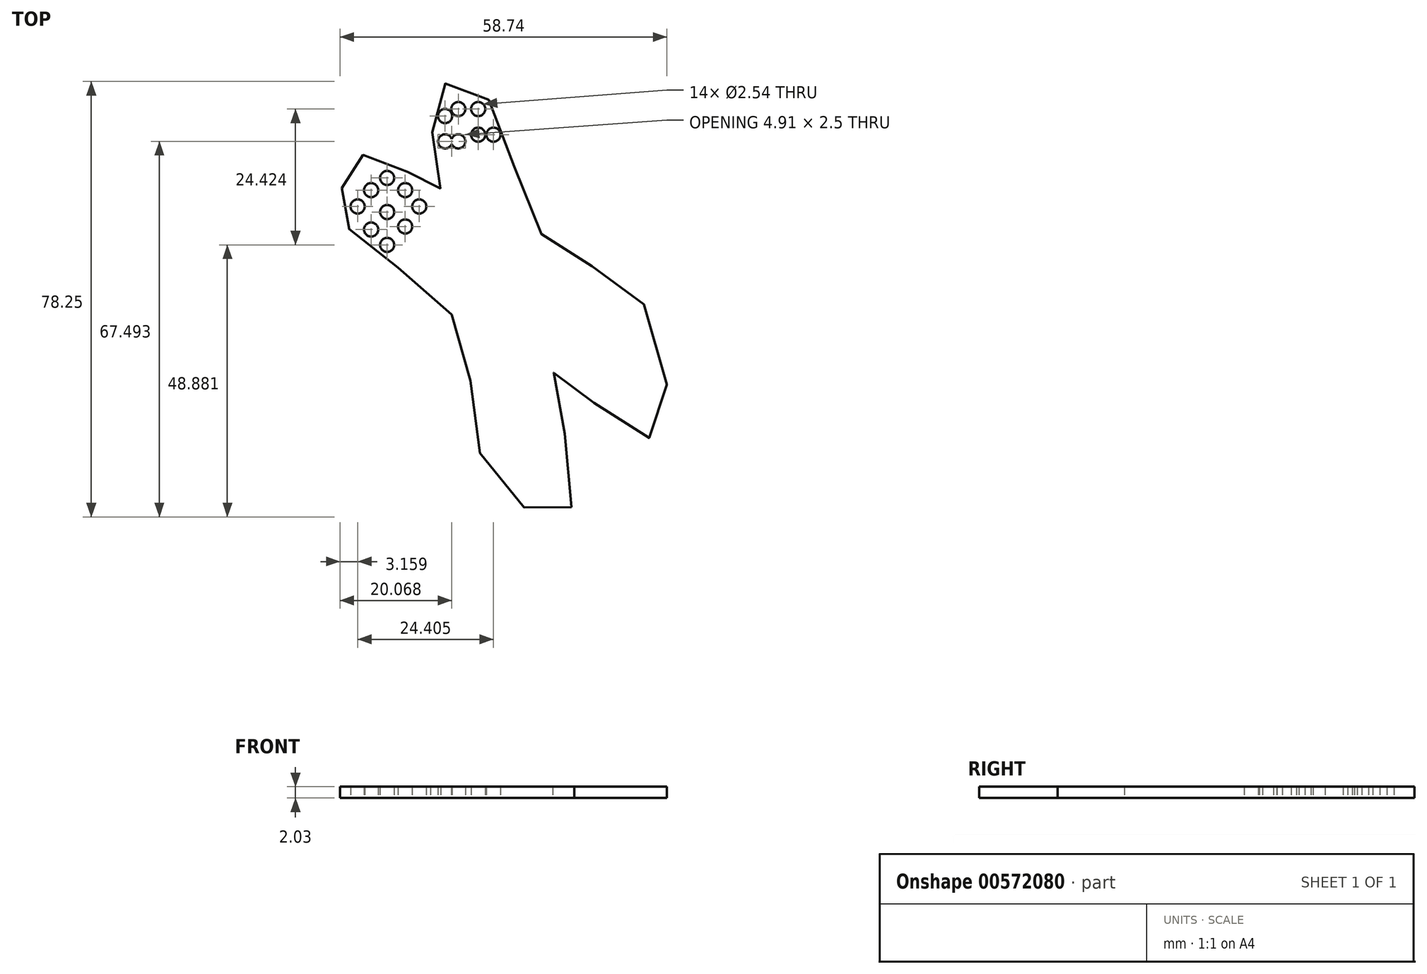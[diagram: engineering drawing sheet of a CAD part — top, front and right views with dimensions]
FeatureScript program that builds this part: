
annotation { "Feature Type Name" : "Feature", "Feature Type Description" : "" }
export const myFeature = defineFeature(function(context is Context, id is Id, definition is map)
    precondition{}
    {
        {
            var Q0;
            Q0=qCreatedBy(makeId("Top.planeOp"),FACE);
            var sketch = newSketch(context, id + "F0", { "sketchPlane" : qUnion([Q0])});
            skFitSpline(sketch, "E0", {"points": [v(-85.83, -33.28) * mm, v(-100.36, -27.64) * mm, v(-106.5, 0) * mm, v(-125.54, 16.41) * mm, v(-126.5, 25.88) * mm, v(-120.74, 30.2) * mm, v(-109.65, 23.59) * mm, v(-110.67, 40.53) * mm, v(-101.77, 41.16) * mm, v(-90.9, 15.39) * mm, v(-72.87, 3.25) * mm, v(-72.2, -20.9) * mm, v(-88.85, -8.98) * mm, v(-85.83, -33.28) * mm]});
            skPoint(sketch, "E1", {"position": v(-124.24, 20.75) * mm});
            skPoint(sketch, "E2", {"position": v(-121.82, 23.68) * mm});
            skPoint(sketch, "E3", {"position": v(-118.94, 25.88) * mm});
            skPoint(sketch, "E4", {"position": v(-121.82, 16.6) * mm});
            skPoint(sketch, "E5", {"position": v(-118.94, 19.76) * mm});
            skPoint(sketch, "E6", {"position": v(-115.7, 23.68) * mm});
            skPoint(sketch, "E7", {"position": v(-108.52, 37) * mm});
            skPoint(sketch, "E8", {"position": v(-106.15, 38.27) * mm});
            skPoint(sketch, "E9", {"position": v(-102.57, 38.27) * mm});
            skPoint(sketch, "E10", {"position": v(-108.52, 32.45) * mm});
            skPoint(sketch, "E11", {"position": v(-106.15, 32.45) * mm});
            skPoint(sketch, "E12", {"position": v(-102.57, 33.65) * mm});
            skPoint(sketch, "E13", {"position": v(-99.84, 33.65) * mm});
            skPoint(sketch, "E14", {"position": v(-118.94, 13.84) * mm});
            skPoint(sketch, "E15", {"position": v(-115.7, 17.14) * mm});
            skPoint(sketch, "E16", {"position": v(-113.17, 20.75) * mm});
            skPoint(sketch, "E17", {"position": v(-113.72, 12.35) * mm});
            skPoint(sketch, "E18", {"position": v(-111.84, 15.66) * mm});
            skPoint(sketch, "E19", {"position": v(-109.39, 18.32) * mm});
            skPoint(sketch, "E20", {"position": v(-110.61, 8.69) * mm});
            skPoint(sketch, "E21", {"position": v(-108.33, 12.3) * mm});
            skPoint(sketch, "E22", {"position": v(-105.8, 16.72) * mm});
            skPoint(sketch, "E23", {"position": v(-101.05, 31.09) * mm});
            skPoint(sketch, "E24", {"position": v(-98.94, 32.74) * mm});
            skPoint(sketch, "E25", {"position": v(-95.42, 33.36) * mm});
            skPoint(sketch, "E26", {"position": v(-100.26, 26.6) * mm});
            skPoint(sketch, "E27", {"position": v(-97.93, 27.02) * mm});
            skPoint(sketch, "E28", {"position": v(-94.62, 28.82) * mm});
            skPoint(sketch, "E29", {"position": v(-91.92, 29.3) * mm});
            skPoint(sketch, "E30", {"position": v(-107.3, 6.47) * mm});
            skPoint(sketch, "E31", {"position": v(-104.67, 10.28) * mm});
            skPoint(sketch, "E32", {"position": v(-102.81, 14.28) * mm});
            skLineSegment(sketch, "E33.0", {"start": v(-94.62, 28.82) * mm, "end": v(-91.92, 29.3) * mm, "construction": true});
            skLineSegment(sketch, "E34.0", {"start": v(-113.72, 12.35) * mm, "end": v(-102.81, 14.28) * mm, "construction": true});
            skLineSegment(sketch, "E35.0", {"start": v(-100.26, 26.6) * mm, "end": v(-97.93, 27.02) * mm, "construction": true});
            skLineSegment(sketch, "E36.0", {"start": v(-111.84, 15.66) * mm, "end": v(-105.8, 16.72) * mm, "construction": true});
            skLineSegment(sketch, "E37.0", {"start": v(-98.94, 32.74) * mm, "end": v(-95.42, 33.36) * mm, "construction": true});
            skLineSegment(sketch, "E38.0", {"start": v(-104.67, 10.28) * mm, "end": v(-105.8, 16.72) * mm, "construction": true});
            skLineSegment(sketch, "E39.0", {"start": v(-107.3, 6.47) * mm, "end": v(-109.39, 18.32) * mm, "construction": true});
            skLineSegment(sketch, "E40.0", {"start": v(-94.62, 28.82) * mm, "end": v(-95.42, 33.36) * mm, "construction": true});
            skLineSegment(sketch, "E41.0", {"start": v(-110.61, 8.69) * mm, "end": v(-111.84, 15.66) * mm, "construction": true});
            skLineSegment(sketch, "E42.0", {"start": v(-100.26, 26.6) * mm, "end": v(-101.05, 31.09) * mm, "construction": true});
            skLineSegment(sketch, "E43.0", {"start": v(-97.93, 27.02) * mm, "end": v(-98.94, 32.74) * mm, "construction": true});
            skSolve(sketch);
        }
        {
            var Q0;
            Q0=makeQuery(id+"F0.imprint","IMPRINT",FACE,{"disambiguationData":[TD([[makeQuery(id+"F0.imprint","IMPRINT",EDGE,{"derivedFrom":sQuery(id+"F0.wireOp",EDGE,"E0")}),-1.0]])]});
            extrude(context, id + "F1", {"entities" : qUnion([Q0]), "depth" : 2.03 * mm, "offsetDistance" : 25.4 * mm});
        }
        {
            var Q0;
            Q0=sQuery(id+"F0.wireOp",VERTEX,"E14");
            var Q1;
            Q1=sQuery(id+"F0.wireOp",VERTEX,"E15");
            var Q2;
            Q2=sQuery(id+"F0.wireOp",VERTEX,"E16");
            var Q3;
            Q3=sQuery(id+"F0.wireOp",VERTEX,"E4");
            var Q4;
            Q4=sQuery(id+"F0.wireOp",VERTEX,"E5");
            var Q5;
            Q5=sQuery(id+"F0.wireOp",VERTEX,"E6");
            var Q6;
            Q6=sQuery(id+"F0.wireOp",VERTEX,"E3");
            var Q7;
            Q7=sQuery(id+"F0.wireOp",VERTEX,"E2");
            var Q8;
            Q8=sQuery(id+"F0.wireOp",VERTEX,"E1");
            var Q9;
            Q9=sQuery(id+"F0.wireOp",VERTEX,"E10");
            var Q10;
            Q10=sQuery(id+"F0.wireOp",VERTEX,"E11");
            var Q11;
            Q11=sQuery(id+"F0.wireOp",VERTEX,"E12");
            var Q12;
            Q12=sQuery(id+"F0.wireOp",VERTEX,"E13");
            var Q13;
            Q13=sQuery(id+"F0.wireOp",VERTEX,"E7");
            var Q14;
            Q14=sQuery(id+"F0.wireOp",VERTEX,"E8");
            var Q15;
            Q15=sQuery(id+"F0.wireOp",VERTEX,"E9");
            var Q16;
            Q16=makeQuery(id+"F1.opExtrude","SWEPT_BODY",BODY,{"disambiguationData":[OSD([sQuery(id+"F0.wireOp",EDGE,"E0")])]});
            hole(context, id + "F2", {"style" : HoleStyle.SIMPLE, "endStyle" : HoleEndStyle.THROUGH, "oppositeDirection" : true, "holeDiameter" : 2.54 * mm, "isTappedThrough" : true, "tappedDepth" : 12.7 * mm, "tapClearance" : 3, "locations" : qUnion([Q0, Q1, Q2, Q3, Q4, Q5, Q6, Q7, Q8, Q9, Q10, Q11, Q12, Q13, Q14, Q15]), "scope" : qUnion([Q16])});
        }
    });
